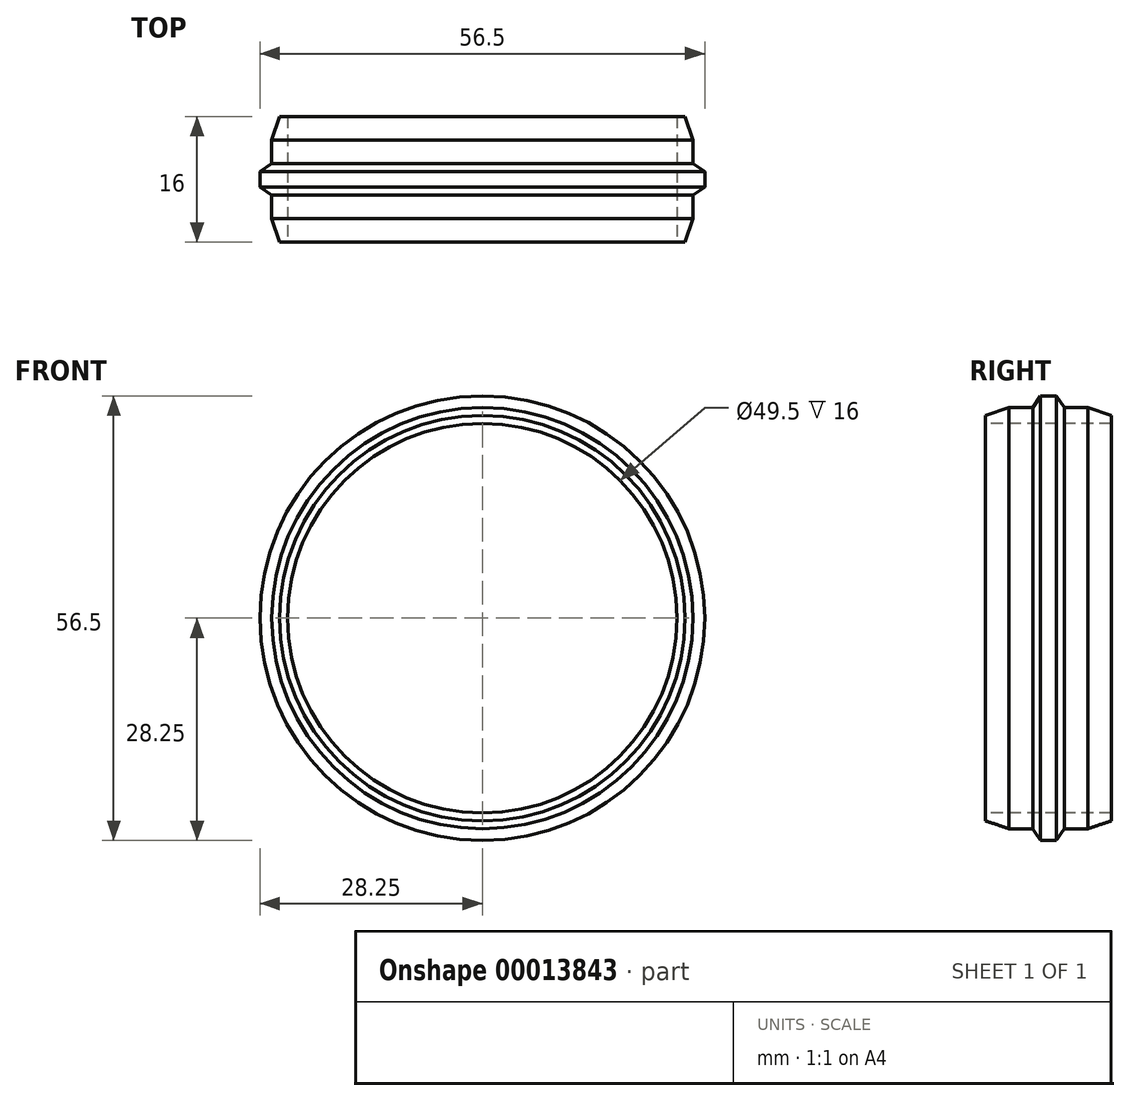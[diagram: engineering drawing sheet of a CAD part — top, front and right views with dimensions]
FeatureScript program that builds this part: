
annotation { "Feature Type Name" : "Feature", "Feature Type Description" : "" }
export const myFeature = defineFeature(function(context is Context, id is Id, definition is map)
    precondition{}
    {
        {
            var Q0;
            Q0=qCreatedBy(makeId("Right.planeOp"),FACE);
            var sketch = newSketch(context, id + "F0", { "sketchPlane" : qUnion([Q0])});
            skLineSegment(sketch, "E0", {"start": v(-8, 24.75) * mm, "end": v(-8, 25.75) * mm});
            skLineSegment(sketch, "E1", {"start": v(-8, 25.75) * mm, "end": v(-5, 26.75) * mm});
            skLineSegment(sketch, "E2", {"start": v(-5, 26.75) * mm, "end": v(-2, 26.75) * mm});
            skLineSegment(sketch, "E3", {"start": v(-2, 26.75) * mm, "end": v(-1, 28.25) * mm});
            skLineSegment(sketch, "E4.MirrorCS", {"start": v(8, 24.75) * mm, "end": v(8, 25.75) * mm});
            skLineSegment(sketch, "E5.MirrorCS", {"start": v(8, 25.75) * mm, "end": v(5, 26.75) * mm});
            skLineSegment(sketch, "E6.MirrorCS", {"start": v(5, 26.75) * mm, "end": v(2, 26.75) * mm});
            skLineSegment(sketch, "E7.MirrorCS", {"start": v(2, 26.75) * mm, "end": v(1, 28.25) * mm});
            skLineSegment(sketch, "E8", {"start": v(-1, 28.25) * mm, "end": v(1, 28.25) * mm});
            skLineSegment(sketch, "E9", {"start": v(-8, 24.75) * mm, "end": v(8, 24.75) * mm});
            skLineSegment(sketch, "E10", {"start": v(-16.18, 0) * mm, "end": v(18.54, 0) * mm, "construction": true});
            skSolve(sketch);
        }
        {
            var Q0;
            Q0 = qSketchRegion(id + "F0", true);
            var Q1;
            Q1=sQuery(id+"F0.wireOp",EDGE,"E10");
            revolve(context, id + "F1", {"entities" : qUnion([Q0]), "axis" : qUnion([Q1]), "revolveType" : RevolveType.FULL});
        }
    });
